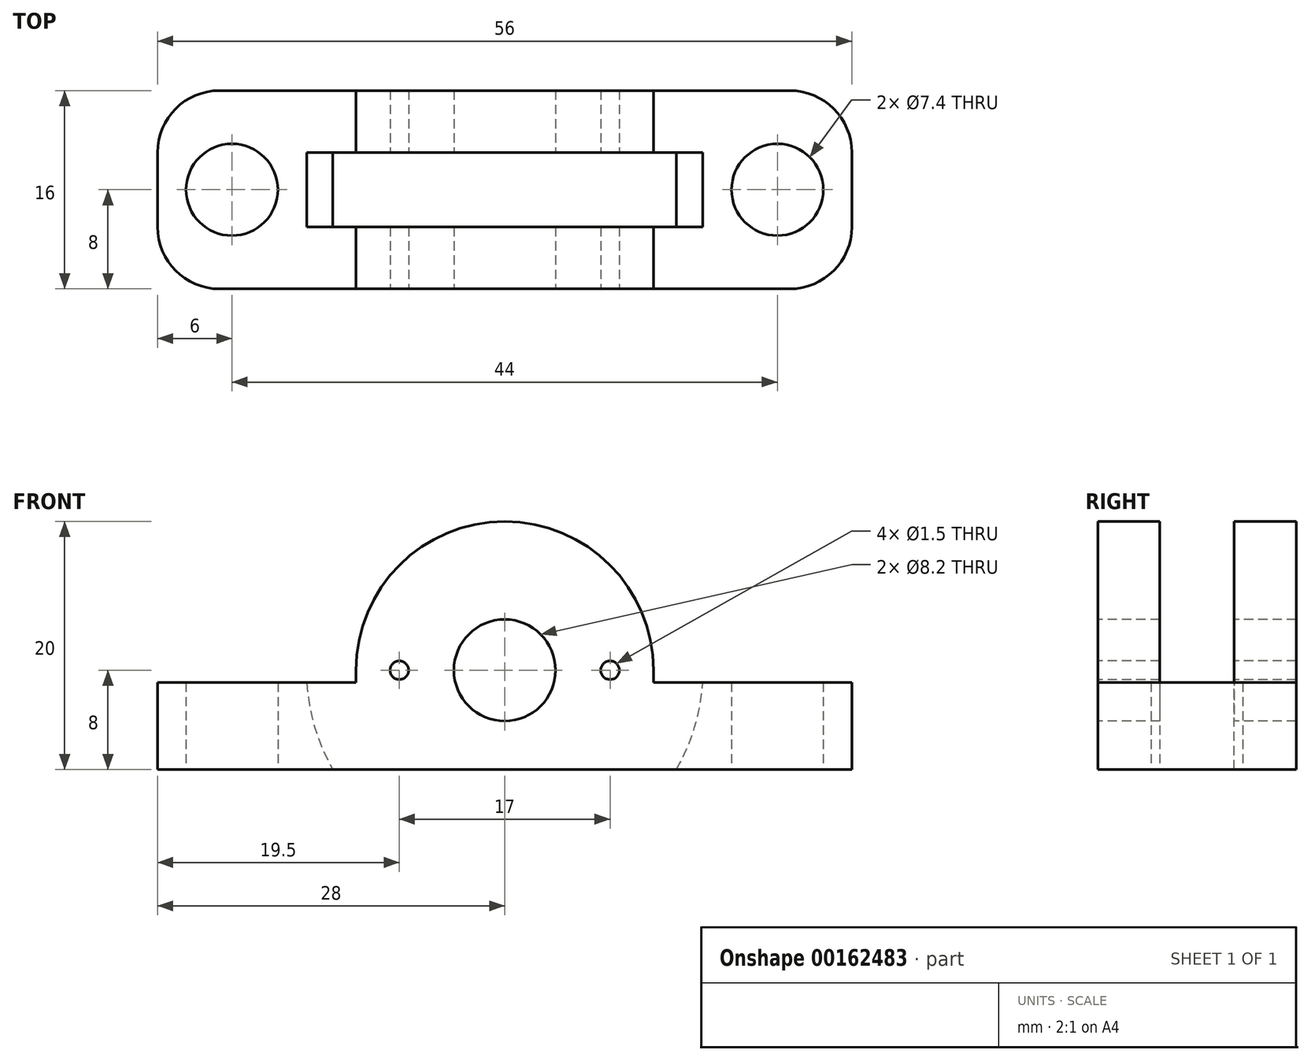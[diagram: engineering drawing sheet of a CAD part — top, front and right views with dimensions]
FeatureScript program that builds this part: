
annotation { "Feature Type Name" : "Feature", "Feature Type Description" : "" }
export const myFeature = defineFeature(function(context is Context, id is Id, definition is map)
    precondition{}
    {
        {
            var Q0;
            Q0=qCreatedBy(makeId("Top.planeOp"),FACE);
            var sketch = newSketch(context, id + "F0", { "sketchPlane" : qUnion([Q0])});
            skCircle(sketch, "E0", {"center": v(-22, 0) * mm, "radius": 3.7 * mm});
            skLineSegment(sketch, "E1", {"start": v(0, 0) * mm, "end": v(0, 20.61) * mm, "construction": true});
            skCircle(sketch, "E2.MirrorC", {"center": v(22, 0) * mm, "radius": 3.7 * mm});
            skLineSegment(sketch, "E3", {"start": v(0, 0) * mm, "end": v(-29.34, 0) * mm, "construction": true});
            skLineSegment(sketch, "E4", {"start": v(-28, 0) * mm, "end": v(-28, 3) * mm});
            skLineSegment(sketch, "E5", {"start": v(-23, 8) * mm, "end": v(0, 8) * mm});
            skPoint(sketch, "E6.visualSharp", {"position": v(-28, 8) * mm});
            skArc(sketch, "E6.filletArc", {"start": v(-23, 8) * mm, "mid": v(-26.54, 6.54) * mm, "end": v(-28, 3) * mm});
            skLineSegment(sketch, "E7.MirrorCS", {"start": v(23, 8) * mm, "end": v(0, 8) * mm});
            skArc(sketch, "E8.MirrorCS", {"start": v(23, 8) * mm, "mid": v(26.54, 6.54) * mm, "end": v(28, 3) * mm});
            skLineSegment(sketch, "E9.MirrorCS", {"start": v(28, 0) * mm, "end": v(28, 3) * mm});
            skLineSegment(sketch, "E10.MirrorCS", {"start": v(-28, 0) * mm, "end": v(-28, -3) * mm});
            skArc(sketch, "E11.MirrorCS", {"start": v(-23, -8) * mm, "mid": v(-26.54, -6.54) * mm, "end": v(-28, -3) * mm});
            skLineSegment(sketch, "E12.MirrorCS", {"start": v(-23, -8) * mm, "end": v(0, -8) * mm});
            skLineSegment(sketch, "E13.MirrorCS", {"start": v(23, -8) * mm, "end": v(0, -8) * mm});
            skArc(sketch, "E14.MirrorCS", {"start": v(23, -8) * mm, "mid": v(26.54, -6.54) * mm, "end": v(28, -3) * mm});
            skLineSegment(sketch, "E15.MirrorCS", {"start": v(28, 0) * mm, "end": v(28, -3) * mm});
            skSolve(sketch);
        }
        {
            var Q0;
            Q0 = qSketchRegion(id + "F0", true);
            extrude(context, id + "F1", {"entities" : qUnion([Q0]), "depth" : 25 * mm});
        }
        {
            var Q0;
            Q0=makeQuery(id+"F1.opExtrude","CAP_FACE",FACE,{"disambiguationData":[OSD([sQuery(id+"F0.wireOp",EDGE,"E0"),sQuery(id+"F0.wireOp",EDGE,"E2.MirrorC"),sQuery(id+"F0.wireOp",EDGE,"E4"),sQuery(id+"F0.wireOp",EDGE,"E5"),sQuery(id+"F0.wireOp",EDGE,"E6.filletArc"),sQuery(id+"F0.wireOp",EDGE,"E7.MirrorCS"),sQuery(id+"F0.wireOp",EDGE,"E8.MirrorCS"),sQuery(id+"F0.wireOp",EDGE,"E9.MirrorCS"),sQuery(id+"F0.wireOp",EDGE,"E10.MirrorCS"),sQuery(id+"F0.wireOp",EDGE,"E11.MirrorCS"),sQuery(id+"F0.wireOp",EDGE,"E12.MirrorCS"),sQuery(id+"F0.wireOp",EDGE,"E13.MirrorCS"),sQuery(id+"F0.wireOp",EDGE,"E14.MirrorCS"),sQuery(id+"F0.wireOp",EDGE,"E15.MirrorCS")])],"isStart":false});
            var sketch = newSketch(context, id + "F2", { "sketchPlane" : qUnion([Q0])});
            skLineSegment(sketch, "E16", {"start": v(0, 0) * mm, "end": v(0, 17.85) * mm, "construction": true});
            skLineSegment(sketch, "E17", {"start": v(0, 0) * mm, "end": v(29.72, 0) * mm, "construction": true});
            skLineSegment(sketch, "E18", {"start": v(0, 3) * mm, "end": v(-12, 3) * mm});
            skLineSegment(sketch, "E19", {"start": v(-12, 3) * mm, "end": v(-12, 8) * mm});
            skLineSegment(sketch, "E20", {"start": v(-12, 8) * mm, "end": v(0, 8) * mm});
            skLineSegment(sketch, "E21.MirrorCS", {"start": v(0, 3) * mm, "end": v(12, 3) * mm});
            skLineSegment(sketch, "E22.MirrorCS", {"start": v(12, 3) * mm, "end": v(12, 8) * mm});
            skLineSegment(sketch, "E23.MirrorCS", {"start": v(12, 8) * mm, "end": v(0, 8) * mm});
            skLineSegment(sketch, "E24.MirrorCS", {"start": v(12, -3) * mm, "end": v(12, -8) * mm});
            skLineSegment(sketch, "E25.MirrorCS", {"start": v(12, -8) * mm, "end": v(0, -8) * mm});
            skLineSegment(sketch, "E26.MirrorCS", {"start": v(-12, -8) * mm, "end": v(0, -8) * mm});
            skLineSegment(sketch, "E27.MirrorCS", {"start": v(-12, -3) * mm, "end": v(-12, -8) * mm});
            skLineSegment(sketch, "E28.MirrorCS", {"start": v(0, -3) * mm, "end": v(-12, -3) * mm});
            skLineSegment(sketch, "E29.MirrorCS", {"start": v(0, -3) * mm, "end": v(12, -3) * mm});
            skLineSegment(sketch, "E30.bottom", {"start": v(-38.9, 24.27) * mm, "end": v(42.67, 24.27) * mm});
            skLineSegment(sketch, "E30.top", {"start": v(-38.9, -25.86) * mm, "end": v(42.67, -25.86) * mm});
            skLineSegment(sketch, "E30.left", {"start": v(-38.9, 24.27) * mm, "end": v(-38.9, -25.86) * mm});
            skLineSegment(sketch, "E30.right", {"start": v(42.67, 24.27) * mm, "end": v(42.67, -25.86) * mm});
            skSolve(sketch);
        }
        {
            var Q0;
            Q0 = qSketchRegion(id + "F2", true);
            extrude(context, id + "F3", {"entities" : qUnion([Q0]), "operationType" : NewBodyOperationType.REMOVE, "oppositeDirection" : true, "depth" : 18 * mm});
        }
        {
            var Q0;
            Q0=makeQuery(id+"F1.opExtrude","SWEPT_FACE",FACE,{"disambiguationData":[OSD([sQuery(id+"F0.wireOp",EDGE,"E12.MirrorCS"),sQuery(id+"F0.wireOp",EDGE,"E13.MirrorCS")])]});
            var sketch = newSketch(context, id + "F4", { "sketchPlane" : qUnion([Q0])});
            skCircle(sketch, "E31", {"center": v(0, 8) * mm, "radius": 4.1 * mm});
            skCircle(sketch, "E32", {"center": v(-8.5, 8) * mm, "radius": 0.75 * mm});
            skLineSegment(sketch, "E33", {"start": v(0, 0) * mm, "end": v(0, 28.7) * mm, "construction": true});
            skPoint(sketch, "E33.endSnap0", {"position": v(0, 25) * mm});
            skCircle(sketch, "E34.MirrorC", {"center": v(8.5, 8) * mm, "radius": 0.75 * mm});
            skArc(sketch, "E35", {"start": v(-12, 8) * mm, "mid": v(0, 20) * mm, "end": v(12, 8) * mm});
            skLineSegment(sketch, "E36", {"start": v(-12, 8) * mm, "end": v(-15.28, 8) * mm});
            skLineSegment(sketch, "E37", {"start": v(-15.28, 8) * mm, "end": v(-15.28, 26.35) * mm});
            skLineSegment(sketch, "E38", {"start": v(-15.28, 26.35) * mm, "end": v(0, 26.35) * mm});
            skLineSegment(sketch, "E39.MirrorCS", {"start": v(15.28, 26.35) * mm, "end": v(0, 26.35) * mm});
            skLineSegment(sketch, "E40.MirrorCS", {"start": v(15.28, 8) * mm, "end": v(15.28, 26.35) * mm});
            skLineSegment(sketch, "E41.MirrorCS", {"start": v(12, 8) * mm, "end": v(15.28, 8) * mm});
            skSolve(sketch);
        }
        {
            var Q0;
            Q0 = qSketchRegion(id + "F4", true);
            extrude(context, id + "F5", {"entities" : qUnion([Q0]), "operationType" : NewBodyOperationType.REMOVE, "endBound" : BoundingType.THROUGH_ALL, "oppositeDirection" : true, "depth" : 25 * mm});
        }
        {
            var Q0;
            Q0=makeQuery(id+"F3.boolean.opBoolean","COPY",FACE,{"derivedFrom":makeQuery(id+"F3.opExtrude","SWEPT_FACE",FACE,{"disambiguationData":[OSD([sQuery(id+"F2.wireOp",EDGE,"E28.MirrorCS"),sQuery(id+"F2.wireOp",EDGE,"E29.MirrorCS")])]})});
            var sketch = newSketch(context, id + "F6", { "sketchPlane" : qUnion([Q0])});
            skCircle(sketch, "E42", {"center": v(0, 8) * mm, "radius": 16 * mm});
            skSolve(sketch);
        }
        {
            var Q0;
            Q0 = qSketchRegion(id + "F6", true);
            extrude(context, id + "F7", {"entities" : qUnion([Q0]), "operationType" : NewBodyOperationType.REMOVE, "depth" : 6 * mm});
        }
    });
